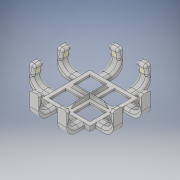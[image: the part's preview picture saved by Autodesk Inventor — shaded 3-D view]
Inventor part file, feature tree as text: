
AUTODESK INVENTOR PART (.ipt)
format: ipt  version: 2018 (Build 220112000, 112)  size: 1,210,880 bytes
history: native  units: in
note: dims shown in document units (in); Inventor stores cm internally (conversion verified against a paired STEP export)
features: other x10, extrude x6, fillet x5, mirror x3, sketch x3, move_body x2, pattern_circular x2, projected_geometry x2, plane x1, chamfer x1, boolean_combine x1, delete_face x1
ambient origin geometry x8: Origin, YZ Plane, XZ Plane, XY Plane, X Axis, Y Axis, Z Axis, Center Point
bodies: Solid2 (feature_tree), Solid5 (feature_tree), Solid6 (feature_tree)
feature tree (37):
  other  "Case Top.ipt"
  other  "Case Bottom.ipt"
  other  "Case Bottom"
  plane  "Work Plane1"
  extrude  "Extrusion3"  Depth=1.5in
  extrude  "Extrusion2"  Depth=1.0in
  fillet  "Fillet7"  Radius=0.02in
  chamfer  "Chamfer1"  Distance=0.225in
  extrude  "Extrusion4"  Depth=1.3in
  mirror  "Mirror1"
  move_body  "Move Body1"
  move_body  "Move Body2"
  extrude  "Extrusion7"  Depth=1.3in
  fillet  "Fillet9"  Radius=0.2in
  pattern_circular  "Circular Pattern2"  [2 undecoded]
  other  "Side holder sketch"
  extrude  "Extrusion5"  Depth=0.125in TaperAngle=0.0deg
  extrude  "Extrusion6"  Depth=0.55in
  boolean_combine  "Combine1"
  delete_face  "Delete Face1"
  fillet  "Fillet1"  Radius=0.02in
  fillet  "Fillet11"  Radius=0.475in
  fillet  "Fillet12"  Radius=0.075in
  mirror  "Mirror2"
  mirror  "Mirror3"
  pattern_circular  "Circular Pattern1"  [2 undecoded]
  sketch  "Sketch1"  dims[d0=1.5in d1=1.5in]
  sketch  "Sketch2"  dims[d2=0.02in d3=1.0in d4=0.02in]
  sketch  "Sketch3"  dims[d5=1.0in d8=0.225in d9=0.0in d20=1.3in d21=1.3in d23=0.2in d24=0.2in d25=0.125in d26=0.0in d27=0.55in d28=0.02in d29=-0.1718in d30=0.475in d31=0.075in d32=0.5in d35=0.5in d36=0.0in d37=0.25in d38=0.0in d39=0.3937in d40=180.0deg d41=0.0in d42=0.7in d43=0.0in d44=0.25in d46=0.7874in d47=90.0deg d49=0.3937in d50=180.0deg d51=0.0in d52=0.7in d53=0.0in d54=0.125in d55=0.3in d60=0.0833in d61=0.6in d62=0.075in d63=0.99in d64=0.125in d65=0.125in d66=1.0in d67=0.195in d68=0.175in d69=0.0625in d70=0.25in d71=0.0in d72=0.7874in d73=90.0deg d76=0.0625in d78=0.0625in d79=0.0625in d80=0.1in d81=0.125in d82=45.0deg]
  projected_geometry  "Projected Loop1"
  projected_geometry  "Projected Loop2"
  other  "TaggingFeature1"
  other  "TaggingFeature2"
  other  "Top compressor sketch"
  other  "Solid2::Case Bottom.ipt"
  other  "Solid3::Case Top.ipt"
  other  "Case Top"
note: 4 required parameter values undecoded (feature->parameter linkage not recoverable at this tier; creation-order binding heuristic only, values carry confidence <= 0.55)
